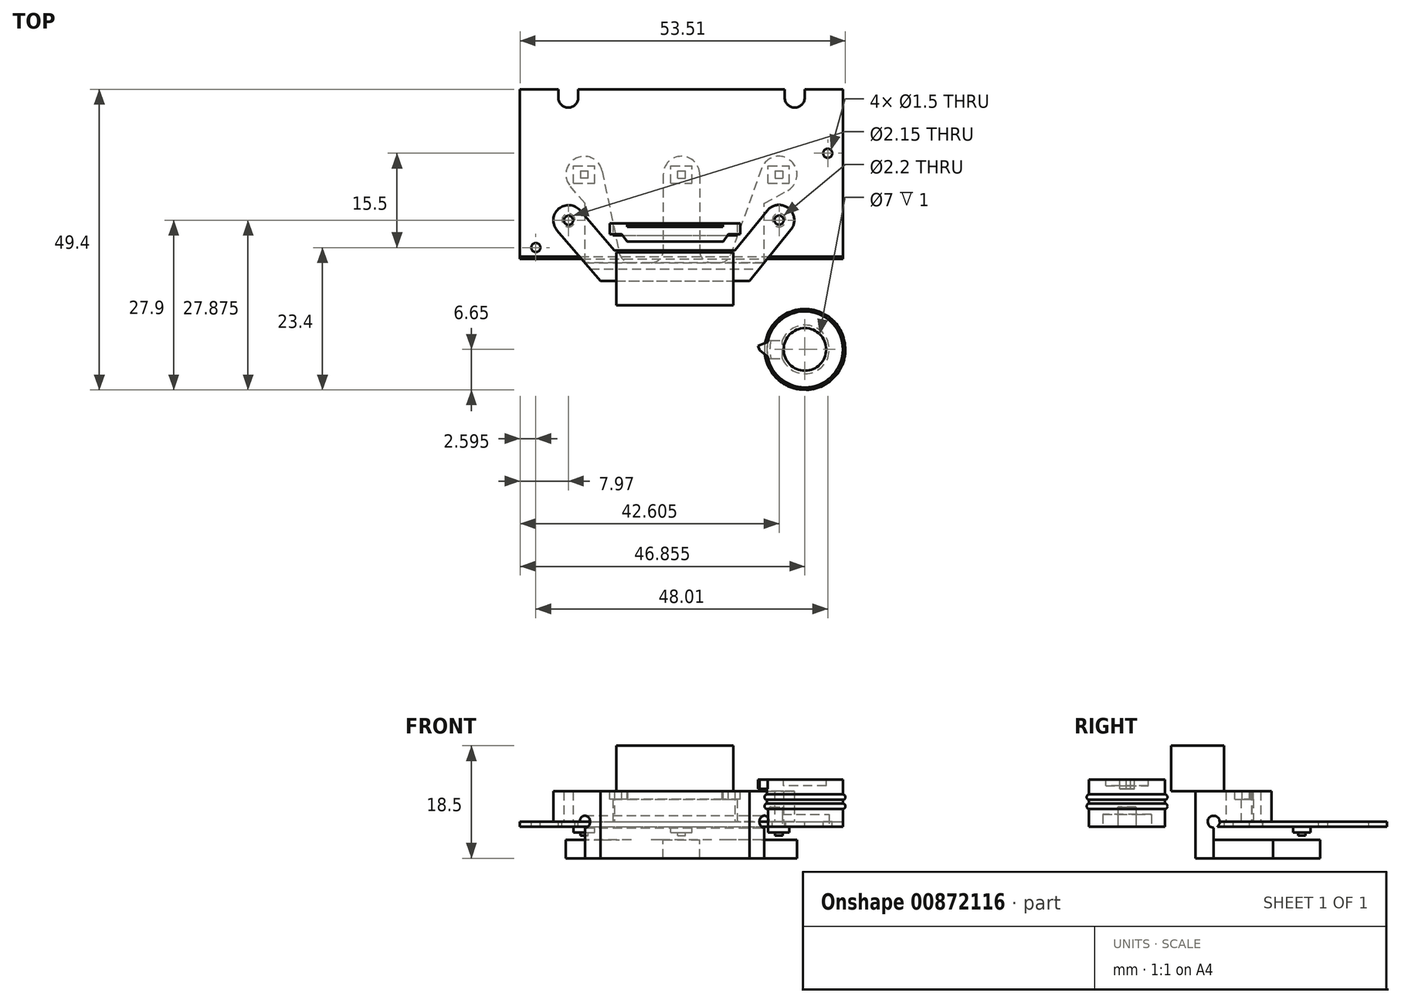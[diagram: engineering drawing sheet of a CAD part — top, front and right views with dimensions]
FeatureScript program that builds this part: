
annotation { "Feature Type Name" : "Feature", "Feature Type Description" : "" }
export const myFeature = defineFeature(function(context is Context, id is Id, definition is map)
    precondition{}
    {
        {
            var Q0;
            Q0=qCreatedBy(makeId("Top.planeOp"),FACE);
            var sketch = newSketch(context, id + "F0", { "sketchPlane" : qUnion([Q0])});
            skLineSegment(sketch, "E0.bottom", {"start": v(-26.56, 14) * mm, "end": v(26.56, 14) * mm});
            skLineSegment(sketch, "E0.top", {"start": v(-26.56, -14) * mm, "end": v(26.55, -14) * mm});
            skLineSegment(sketch, "E0.left", {"start": v(-26.55, 14) * mm, "end": v(-26.56, -14) * mm});
            skLineSegment(sketch, "E0.right", {"start": v(26.56, 14) * mm, "end": v(26.55, -14) * mm});
            skLineSegment(sketch, "E1", {"start": v(-26.56, 14) * mm, "end": v(26.56, -14) * mm, "construction": true});
            skSolve(sketch);
        }
        {
            var Q0;
            Q0 = qSketchRegion(id + "F0", true);
            extrude(context, id + "F1", {"entities" : qUnion([Q0]), "depth" : .8 * mm, "offsetDistance" : 25 * mm});
        }
        {
            var Q0;
            Q0=makeQuery(id+"F1.opExtrude","CAP_FACE",FACE,{"disambiguationData":[OSD([sQuery(id+"F0.wireOp",EDGE,"E0.bottom"),sQuery(id+"F0.wireOp",EDGE,"E0.top"),sQuery(id+"F0.wireOp",EDGE,"E0.left"),sQuery(id+"F0.wireOp",EDGE,"E0.right")])],"isStart":false});
            var sketch = newSketch(context, id + "F2", { "sketchPlane" : qUnion([Q0])});
            skArc(sketch, "E2", {"start": v(16.99, 12.63) * mm, "mid": v(18.62, 11) * mm, "end": v(20.26, 12.63) * mm});
            skArc(sketch, "E3", {"start": v(-20.26, 12.63) * mm, "mid": v(-18.62, 11) * mm, "end": v(-16.98, 12.63) * mm});
            skCircle(sketch, "E4", {"center": v(-18.58, -7.53) * mm, "radius": 1.07 * mm});
            skCircle(sketch, "E5", {"center": v(16.06, -7.5) * mm, "radius": 1.1 * mm});
            skCircle(sketch, "E6", {"center": v(24.05, 3.5) * mm, "radius": 0.75 * mm});
            skCircle(sketch, "E7", {"center": v(-23.96, -12) * mm, "radius": 0.75 * mm});
            skLineSegment(sketch, "E8", {"start": v(16.58, 11) * mm, "end": v(20.98, 11) * mm, "construction": true});
            skLineSegment(sketch, "E9", {"start": v(16.99, 14) * mm, "end": v(20.26, 14) * mm});
            skLineSegment(sketch, "E10.trimOffspring", {"start": v(16.99, 12.63) * mm, "end": v(16.99, 14) * mm});
            skLineSegment(sketch, "E11.trimOffspring", {"start": v(20.26, 12.63) * mm, "end": v(20.26, 14) * mm});
            skLineSegment(sketch, "E12", {"start": v(-16.98, 14) * mm, "end": v(-16.98, 12.63) * mm});
            skLineSegment(sketch, "E13", {"start": v(-20.26, 14) * mm, "end": v(-20.26, 12.63) * mm});
            skLineSegment(sketch, "E14", {"start": v(-20.26, 14) * mm, "end": v(-16.98, 14) * mm});
            skLineSegment(sketch, "E15", {"start": v(24.8, 5.15) * mm, "end": v(24.8, 1.76) * mm, "construction": true});
            skLineSegment(sketch, "E16", {"start": v(22, 2.75) * mm, "end": v(26.48, 2.75) * mm, "construction": true});
            skLineSegment(sketch, "E17", {"start": v(10.95, -8.6) * mm, "end": v(16.92, -8.6) * mm, "construction": true});
            skLineSegment(sketch, "E18", {"start": v(17.16, -5.77) * mm, "end": v(17.16, -10.33) * mm, "construction": true});
            skLineSegment(sketch, "E19", {"start": v(-19.66, -5.92) * mm, "end": v(-19.66, -10.32) * mm, "construction": true});
            skLineSegment(sketch, "E20", {"start": v(-21.28, -8.6) * mm, "end": v(-15.46, -8.6) * mm, "construction": true});
            skLineSegment(sketch, "E21", {"start": v(-24.7, -11.2) * mm, "end": v(-24.7, -13.47) * mm, "construction": true});
            skLineSegment(sketch, "E22", {"start": v(-25.52, -12.75) * mm, "end": v(-23.02, -12.75) * mm, "construction": true});
            skSolve(sketch);
        }
        {
            var Q0;
            Q0 = qSketchRegion(id + "F2", true);
            extrude(context, id + "F3", {"entities" : qUnion([Q0]), "operationType" : NewBodyOperationType.REMOVE, "endBound" : BoundingType.THROUGH_ALL, "oppositeDirection" : true, "depth" : 25 * mm, "offsetDistance" : 25 * mm});
        }
        {
            var Q0;
            Q0=makeQuery(id+"F1.opExtrude","CAP_FACE",FACE,{"disambiguationData":[OSD([sQuery(id+"F0.wireOp",EDGE,"E0.bottom"),sQuery(id+"F0.wireOp",EDGE,"E0.top"),sQuery(id+"F0.wireOp",EDGE,"E0.left"),sQuery(id+"F0.wireOp",EDGE,"E0.right")])],"isStart":false});
            var sketch = newSketch(context, id + "F4", { "sketchPlane" : qUnion([Q0])});
            skLineSegment(sketch, "E23.bottom", {"start": v(-11.26, -8) * mm, "end": v(9.14, -8) * mm});
            skLineSegment(sketch, "E23.top", {"start": v(-11.26, -10) * mm, "end": v(9.14, -10) * mm});
            skLineSegment(sketch, "E23.left", {"start": v(-11.26, -8) * mm, "end": v(-11.26, -10) * mm});
            skLineSegment(sketch, "E23.right", {"start": v(9.14, -8) * mm, "end": v(9.14, -10) * mm});
            skSolve(sketch);
        }
        {
            var Q0;
            Q0 = qSketchRegion(id + "F4", true);
            extrude(context, id + "F5", {"entities" : qUnion([Q0]), "depth" : 5 * mm, "offsetDistance" : 25 * mm});
        }
        {
            var Q0;
            Q0=makeQuery(id+"F5.opExtrude","CAP_FACE",FACE,{"disambiguationData":[OSD([sQuery(id+"F4.wireOp",EDGE,"E23.bottom"),sQuery(id+"F4.wireOp",EDGE,"E23.top"),sQuery(id+"F4.wireOp",EDGE,"E23.left"),sQuery(id+"F4.wireOp",EDGE,"E23.right")])],"isStart":false});
            var sketch = newSketch(context, id + "F6", { "sketchPlane" : qUnion([Q0])});
            skLineSegment(sketch, "E24.bottom", {"start": v(-11.26, -10) * mm, "end": v(9.14, -10) * mm});
            skLineSegment(sketch, "E24.top", {"start": v(-8.8, -8.5) * mm, "end": v(6.7, -8.5) * mm});
            skLineSegment(sketch, "E24.left", {"start": v(-11.26, -10) * mm, "end": v(-11.26, -8.5) * mm});
            skLineSegment(sketch, "E24.right", {"start": v(9.14, -10) * mm, "end": v(9.14, -8.5) * mm});
            skLineSegment(sketch, "E25.top", {"start": v(-8.8, -8) * mm, "end": v(-11.26, -8) * mm});
            skLineSegment(sketch, "E25.left", {"start": v(-8.8, -8.5) * mm, "end": v(-8.8, -8) * mm});
            skLineSegment(sketch, "E25.right", {"start": v(-11.26, -8.5) * mm, "end": v(-11.26, -8) * mm});
            skLineSegment(sketch, "E26.bottom", {"start": v(9.14, -8) * mm, "end": v(6.7, -8) * mm});
            skLineSegment(sketch, "E26.left", {"start": v(9.14, -8) * mm, "end": v(9.14, -8.5) * mm});
            skLineSegment(sketch, "E26.right", {"start": v(6.7, -8) * mm, "end": v(6.7, -8.5) * mm});
            skSolve(sketch);
        }
        {
            var Q0;
            Q0 = qSketchRegion(id + "F6", true);
            extrude(context, id + "F7", {"entities" : qUnion([Q0]), "operationType" : NewBodyOperationType.REMOVE, "oppositeDirection" : true, "depth" : 1.3 * mm, "offsetDistance" : 25 * mm});
        }
        {
            var Q0;
            Q0=makeQuery(id+"F5.opExtrude","CAP_FACE",FACE,{"disambiguationData":[OSD([sQuery(id+"F4.wireOp",EDGE,"E23.bottom"),sQuery(id+"F4.wireOp",EDGE,"E23.top"),sQuery(id+"F4.wireOp",EDGE,"E23.left"),sQuery(id+"F4.wireOp",EDGE,"E23.right")])],"isStart":false});
            var sketch = newSketch(context, id + "F8", { "sketchPlane" : qUnion([Q0])});
            skLineSegment(sketch, "E27.bottom", {"start": v(-11.8, -8) * mm, "end": v(-1.06, -8) * mm});
            skLineSegment(sketch, "E27.top", {"start": v(-8.96, -11) * mm, "end": v(6.84, -11) * mm});
            skLineSegment(sketch, "E27.left", {"start": v(-11.8, -8) * mm, "end": v(-11.8, -9.8) * mm});
            skLineSegment(sketch, "E27.right", {"start": v(9.7, -8) * mm, "end": v(9.7, -9.8) * mm});
            skLineSegment(sketch, "E28", {"start": v(-1.06, -10) * mm, "end": v(-1.06, -6.45) * mm, "construction": true});
            skLineSegment(sketch, "E29.0", {"start": v(-8.9, -8.6) * mm, "end": v(6.8, -8.6) * mm});
            skLineSegment(sketch, "E30.0", {"start": v(-8.9, -8.6) * mm, "end": v(-8.9, -8) * mm});
            skLineSegment(sketch, "E31.0", {"start": v(6.8, -8) * mm, "end": v(6.8, -8.6) * mm});
            skLineSegment(sketch, "E32.trimOffspring", {"start": v(6.8, -8) * mm, "end": v(9.7, -8) * mm});
            skLineSegment(sketch, "E33", {"start": v(9.7, -9.8) * mm, "end": v(7.7, -9.8) * mm});
            skLineSegment(sketch, "E34", {"start": v(7.7, -9.8) * mm, "end": v(6.84, -11) * mm});
            skLineSegment(sketch, "E35.MirrorCS", {"start": v(-11.8, -9.8) * mm, "end": v(-9.8, -9.8) * mm});
            skLineSegment(sketch, "E36.MirrorCS", {"start": v(-9.8, -9.8) * mm, "end": v(-8.96, -11) * mm});
            skSolve(sketch);
        }
        {
            var Q0;
            Q0 = qSketchRegion(id + "F8", true);
            var Q1;
            Q1=makeQuery(id+"F7.boolean.opBoolean","COPY",FACE,{"derivedFrom":makeQuery(id+"F7.opExtrude","CAP_FACE",FACE,{"disambiguationData":[OSD([sQuery(id+"F6.wireOp",EDGE,"E24.bottom"),sQuery(id+"F6.wireOp",EDGE,"E24.top"),sQuery(id+"F6.wireOp",EDGE,"E24.left"),sQuery(id+"F6.wireOp",EDGE,"E24.right"),sQuery(id+"F6.wireOp",EDGE,"E25.top"),sQuery(id+"F6.wireOp",EDGE,"E25.left"),sQuery(id+"F6.wireOp",EDGE,"E25.right"),sQuery(id+"F6.wireOp",EDGE,"E26.bottom"),sQuery(id+"F6.wireOp",EDGE,"E26.left"),sQuery(id+"F6.wireOp",EDGE,"E26.right")])],"isStart":false})});
            extrude(context, id + "F9", {"entities" : qUnion([Q0]), "endBound" : BoundingType.UP_TO_SURFACE, "oppositeDirection" : true, "depth" : 25 * mm, "endBoundEntityFace" : qUnion([Q1]), "offsetDistance" : 25 * mm});
        }
        {
            var Q0;
            Q0=makeQuery(id+"F1.opExtrude","CAP_FACE",FACE,{"disambiguationData":[OSD([sQuery(id+"F0.wireOp",EDGE,"E0.bottom"),sQuery(id+"F0.wireOp",EDGE,"E0.top"),sQuery(id+"F0.wireOp",EDGE,"E0.left"),sQuery(id+"F0.wireOp",EDGE,"E0.right")])],"isStart":true});
            var sketch = newSketch(context, id + "F10", { "sketchPlane" : qUnion([Q0])});
            skLineSegment(sketch, "E37.bottom", {"start": v(-17.75, 1.45) * mm, "end": v(-14.26, 1.45) * mm});
            skLineSegment(sketch, "E37.top", {"start": v(-17.75, -1.45) * mm, "end": v(-14.26, -1.45) * mm});
            skLineSegment(sketch, "E37.left", {"start": v(-17.75, 1.45) * mm, "end": v(-17.75, -1.45) * mm});
            skLineSegment(sketch, "E37.right", {"start": v(-14.26, 1.45) * mm, "end": v(-14.26, -1.45) * mm});
            skLineSegment(sketch, "E38.bottom", {"start": v(-1.75, 1.45) * mm, "end": v(1.75, 1.45) * mm});
            skLineSegment(sketch, "E38.top", {"start": v(-1.75, -1.45) * mm, "end": v(1.75, -1.45) * mm});
            skLineSegment(sketch, "E38.left", {"start": v(-1.75, 1.45) * mm, "end": v(-1.75, -1.45) * mm});
            skLineSegment(sketch, "E38.right", {"start": v(1.75, 1.45) * mm, "end": v(1.75, -1.45) * mm});
            skLineSegment(sketch, "E39.bottom", {"start": v(14.26, 1.45) * mm, "end": v(17.75, 1.45) * mm});
            skLineSegment(sketch, "E39.top", {"start": v(14.26, -1.45) * mm, "end": v(17.75, -1.45) * mm});
            skLineSegment(sketch, "E39.left", {"start": v(14.26, 1.45) * mm, "end": v(14.26, -1.45) * mm});
            skLineSegment(sketch, "E39.right", {"start": v(17.75, 1.45) * mm, "end": v(17.75, -1.45) * mm});
            skLineSegment(sketch, "E40", {"start": v(-1.75, 1.45) * mm, "end": v(1.75, -1.45) * mm, "construction": true});
            skSolve(sketch);
        }
        {
            var Q0;
            Q0 = qSketchRegion(id + "F10", true);
            extrude(context, id + "F11", {"entities" : qUnion([Q0]), "depth" : 1 * mm, "offsetDistance" : 25 * mm});
        }
        {
            var Q0;
            Q0=makeQuery(id+"F11.opExtrude","CAP_FACE",FACE,{"disambiguationData":[OSD([sQuery(id+"F10.wireOp",EDGE,"E37.bottom"),sQuery(id+"F10.wireOp",EDGE,"E37.top"),sQuery(id+"F10.wireOp",EDGE,"E37.left"),sQuery(id+"F10.wireOp",EDGE,"E37.right")])],"isStart":false});
            var sketch = newSketch(context, id + "F12", { "sketchPlane" : qUnion([Q0])});
            skPoint(sketch, "E41.firstSnap0", {"position": v(-14.26, 0) * mm});
            skLineSegment(sketch, "E41.top", {"start": v(-16.63, -0.63) * mm, "end": v(-15.38, -0.63) * mm});
            skLineSegment(sketch, "E41.right", {"start": v(-15.38, 0.62) * mm, "end": v(-15.38, -0.63) * mm});
            skLineSegment(sketch, "E42", {"start": v(-17.75, 1.45) * mm, "end": v(-14.26, -1.45) * mm, "construction": true});
            skLineSegment(sketch, "E43", {"start": v(-15.38, 0.62) * mm, "end": v(-16.63, -0.63) * mm, "construction": true});
            skPoint(sketch, "E44", {"position": v(-16, 0) * mm});
            skLineSegment(sketch, "E45", {"start": v(-15.38, 0.62) * mm, "end": v(-16.63, 0.62) * mm});
            skLineSegment(sketch, "E46", {"start": v(-16.63, -0.63) * mm, "end": v(-16.63, 0.62) * mm});
            skLineSegment(sketch, "E47.bottom", {"start": v(-0.62, 0.62) * mm, "end": v(0.62, 0.62) * mm});
            skLineSegment(sketch, "E47.top", {"start": v(-0.62, -0.62) * mm, "end": v(0.62, -0.62) * mm});
            skLineSegment(sketch, "E47.left", {"start": v(-0.62, 0.62) * mm, "end": v(-0.62, -0.62) * mm});
            skLineSegment(sketch, "E47.right", {"start": v(0.62, 0.62) * mm, "end": v(0.62, -0.62) * mm});
            skLineSegment(sketch, "E48", {"start": v(-0.62, 0.62) * mm, "end": v(0.62, -0.62) * mm, "construction": true});
            skLineSegment(sketch, "E49", {"start": v(14.26, 1.45) * mm, "end": v(17.75, -1.45) * mm, "construction": true});
            skLineSegment(sketch, "E50.bottom", {"start": v(15.38, -0.63) * mm, "end": v(16.63, -0.63) * mm});
            skLineSegment(sketch, "E50.top", {"start": v(15.38, 0.62) * mm, "end": v(16.63, 0.62) * mm});
            skLineSegment(sketch, "E50.left", {"start": v(15.38, -0.63) * mm, "end": v(15.38, 0.62) * mm});
            skLineSegment(sketch, "E50.right", {"start": v(16.63, -0.63) * mm, "end": v(16.63, 0.62) * mm});
            skLineSegment(sketch, "E51", {"start": v(15.38, -0.63) * mm, "end": v(16.63, 0.62) * mm, "construction": true});
            skPoint(sketch, "E52", {"position": v(16, 0) * mm});
            skSolve(sketch);
        }
        {
            var Q0;
            Q0 = qSketchRegion(id + "F12", true);
            extrude(context, id + "F13", {"entities" : qUnion([Q0]), "depth" : .5 * mm, "offsetDistance" : 25 * mm});
        }
        {
            var Q0;
            Q0=makeQuery(id+"F1.opExtrude","CAP_FACE",FACE,{"disambiguationData":[OSD([sQuery(id+"F0.wireOp",EDGE,"E0.bottom"),sQuery(id+"F0.wireOp",EDGE,"E0.top"),sQuery(id+"F0.wireOp",EDGE,"E0.left"),sQuery(id+"F0.wireOp",EDGE,"E0.right")])],"isStart":true});
            var sketch = newSketch(context, id + "F14", { "sketchPlane" : qUnion([Q0])});
            skCircle(sketch, "E53", {"center": v(20.3, 28.75) * mm, "radius": 6.25 * mm});
            skLineSegment(sketch, "E54", {"start": v(14.4, 22.5) * mm, "end": v(31.08, 22.5) * mm, "construction": true});
            skLineSegment(sketch, "E55", {"start": v(26.55, 37.01) * mm, "end": v(26.55, 25.34) * mm, "construction": true});
            skSolve(sketch);
        }
        {
            var Q0;
            Q0 = qSketchRegion(id + "F14", true);
            extrude(context, id + "F15", {"entities" : qUnion([Q0]), "oppositeDirection" : true, "depth" : 7.7 * mm, "offsetDistance" : 25 * mm});
        }
        {
            var Q0;
            Q0=makeQuery(id+"F15.opExtrude","CAP_FACE",FACE,{"disambiguationData":[OSD([sQuery(id+"F14.wireOp",EDGE,"E53")])],"isStart":false});
            var sketch = newSketch(context, id + "F16", { "sketchPlane" : qUnion([Q0])});
            skCircle(sketch, "E56", {"center": v(20.3, -28.75) * mm, "radius": 3.5 * mm});
            skSolve(sketch);
        }
        {
            var Q0;
            Q0 = qSketchRegion(id + "F16", true);
            extrude(context, id + "F17", {"entities" : qUnion([Q0]), "operationType" : NewBodyOperationType.REMOVE, "oppositeDirection" : true, "depth" : 1 * mm, "offsetDistance" : 25 * mm});
        }
        {
            var Q0;
            Q0=makeQuery(id+"F15.opExtrude","CAP_FACE",FACE,{"disambiguationData":[OSD([sQuery(id+"F14.wireOp",EDGE,"E53")])],"isStart":true});
            var sketch = newSketch(context, id + "F18", { "sketchPlane" : qUnion([Q0])});
            skCircle(sketch, "E57", {"center": v(20.3, 28.75) * mm, "radius": 4 * mm});
            skSolve(sketch);
        }
        {
            var Q0;
            Q0 = qSketchRegion(id + "F18", true);
            extrude(context, id + "F19", {"entities" : qUnion([Q0]), "operationType" : NewBodyOperationType.REMOVE, "oppositeDirection" : true, "depth" : 2 * mm, "offsetDistance" : 25 * mm});
        }
        {
            var Q0;
            Q0=makeQuery(id+"F15.opExtrude","CAP_FACE",FACE,{"disambiguationData":[OSD([sQuery(id+"F14.wireOp",EDGE,"E53")])],"isStart":true});
            var sketch = newSketch(context, id + "F20", { "sketchPlane" : qUnion([Q0])});
            skLineSegment(sketch, "E58.bottom", {"start": v(14.05, 30.25) * mm, "end": v(16.6, 30.25) * mm});
            skLineSegment(sketch, "E58.top", {"start": v(14.05, 27.25) * mm, "end": v(16.6, 27.25) * mm});
            skLineSegment(sketch, "E58.left", {"start": v(14.05, 30.25) * mm, "end": v(14.05, 27.25) * mm});
            skLineSegment(sketch, "E58.right", {"start": v(16.6, 30.25) * mm, "end": v(16.6, 27.25) * mm});
            skPoint(sketch, "E59", {"position": v(20.3, 28.75) * mm});
            skLineSegment(sketch, "E60", {"start": v(16.6, 28.75) * mm, "end": v(20.3, 28.75) * mm});
            skSolve(sketch);
        }
        {
            var Q0;
            Q0 = qSketchRegion(id + "F20", true);
            extrude(context, id + "F21", {"entities" : qUnion([Q0]), "operationType" : NewBodyOperationType.REMOVE, "oppositeDirection" : true, "depth" : 3.2 * mm, "offsetDistance" : 25 * mm});
        }
        {
            var Q0;
            Q0=makeQuery(id+"F15.opExtrude","CAP_FACE",FACE,{"disambiguationData":[OSD([sQuery(id+"F14.wireOp",EDGE,"E53")])],"isStart":false});
            var sketch = newSketch(context, id + "F22", { "sketchPlane" : qUnion([Q0])});
            skArc(sketch, "E61.0", {"start": v(14.17, -27.55) * mm, "mid": v(14.05, -28.75) * mm, "end": v(14.17, -29.95) * mm});
            skLineSegment(sketch, "E62", {"start": v(14.17, -27.55) * mm, "end": v(12.58, -28.16) * mm});
            skLineSegment(sketch, "E63", {"start": v(12.58, -28.16) * mm, "end": v(12.85, -28.87) * mm});
            skLineSegment(sketch, "E64", {"start": v(12.85, -28.87) * mm, "end": v(14.17, -29.95) * mm});
            skSolve(sketch);
        }
        {
            var Q0;
            Q0 = qSketchRegion(id + "F22", true);
            extrude(context, id + "F23", {"entities" : qUnion([Q0]), "operationType" : NewBodyOperationType.ADD, "oppositeDirection" : true, "depth" : 1.5 * mm, "offsetDistance" : 25 * mm});
        }
        {
            var Q0;
            Q0=makeQuery(id+"F23.boolean.opBoolean","MERGE",FACE,{"derivedFrom":[makeQuery(id+"F15.opExtrude","CAP_FACE",FACE,{"disambiguationData":[OSD([sQuery(id+"F14.wireOp",EDGE,"E53")])],"isStart":false}),makeQuery(id+"F23.opExtrude","CAP_FACE",FACE,{"disambiguationData":[OSD([sQuery(id+"F22.wireOp",EDGE,"E61.0"),sQuery(id+"F22.wireOp",EDGE,"E62"),sQuery(id+"F22.wireOp",EDGE,"E63"),sQuery(id+"F22.wireOp",EDGE,"E64")])],"isStart":true})]});
            var sketch = newSketch(context, id + "F24", { "sketchPlane" : qUnion([Q0])});
            skLineSegment(sketch, "E65", {"start": v(20.3, -19.73) * mm, "end": v(20.3, -37.77) * mm});
            skPoint(sketch, "E66", {"position": v(20.3, -28.75) * mm});
            skSolve(sketch);
        }
        {
            var Q0;
            Q0=sQuery(id+"F24.wireOp",EDGE,"E65");
            cPlane(context, id + "F25", {"entities" : qUnion([Q0]), "cplaneType" : CPlaneType.MID_PLANE, "offset" : 25 * mm, "width" : 150 * mm, "height" : 150 * mm});
        }
        {
            var Q0;
            Q0=qCreatedBy(id+"F25.planeOp",FACE);
            var sketch = newSketch(context, id + "F26", { "sketchPlane" : qUnion([Q0])});
            skCircle(sketch, "E67", {"center": v(26.5, 4.85) * mm, "radius": 0.45 * mm});
            skCircle(sketch, "E68", {"center": v(26.5, 3.35) * mm, "radius": 0.45 * mm});
            skLineSegment(sketch, "E69", {"start": v(20.3, 8.47) * mm, "end": v(20.3, -0.14) * mm, "construction": true});
            skLineSegment(sketch, "E70", {"start": v(25.58, 4.4) * mm, "end": v(27.51, 4.4) * mm, "construction": true});
            skSolve(sketch);
        }
        {
            var Q0;
            Q0 = qSketchRegion(id + "F26", true);
            var Q1;
            Q1=sQuery(id+"F26.wireOp",EDGE,"E69");
            revolve(context, id + "F27", {"operationType" : NewBodyOperationType.ADD, "surfaceOperationType" : NewSurfaceOperationType.NEW, "entities" : qUnion([Q0]), "axis" : qUnion([Q1]), "revolveType" : RevolveType.FULL});
        }
        {
            var Q0;
            Q0=makeQuery(id+"F1.opExtrude","CAP_FACE",FACE,{"disambiguationData":[OSD([sQuery(id+"F0.wireOp",EDGE,"E0.bottom"),sQuery(id+"F0.wireOp",EDGE,"E0.top"),sQuery(id+"F0.wireOp",EDGE,"E0.left"),sQuery(id+"F0.wireOp",EDGE,"E0.right")])],"isStart":false});
            var sketch = newSketch(context, id + "F28", { "sketchPlane" : qUnion([Q0])});
            skArc(sketch, "E71", {"start": v(18, -9.07) * mm, "mid": v(17.63, -5.55) * mm, "end": v(14.1, -5.93) * mm});
            skArc(sketch, "E72", {"start": v(-16.68, -5.9) * mm, "mid": v(-20.2, -5.63) * mm, "end": v(-20.48, -9.15) * mm});
            skLineSegment(sketch, "E73.bottom", {"start": v(-11, -12.5) * mm, "end": v(8.8, -12.5) * mm});
            skLineSegment(sketch, "E73.top", {"start": v(-13.3, -17.5) * mm, "end": v(11.2, -17.5) * mm});
            skLineSegment(sketch, "E73.left", {"start": v(-13.3, -12.5) * mm, "end": v(-13.3, -17.5) * mm, "construction": true});
            skLineSegment(sketch, "E73.right", {"start": v(11.2, -12.5) * mm, "end": v(11.2, -17.5) * mm, "construction": true});
            skLineSegment(sketch, "E74", {"start": v(-20.48, -9.15) * mm, "end": v(-13.3, -17.5) * mm});
            skLineSegment(sketch, "E75", {"start": v(-16.68, -5.9) * mm, "end": v(-11, -12.5) * mm});
            skLineSegment(sketch, "E76", {"start": v(-1.06, -17.5) * mm, "end": v(-1.06, -14.15) * mm, "construction": true});
            skLineSegment(sketch, "E77", {"start": v(11.2, -17.5) * mm, "end": v(18, -9.07) * mm});
            skLineSegment(sketch, "E78", {"start": v(14.1, -5.93) * mm, "end": v(8.8, -12.5) * mm});
            skSolve(sketch);
        }
        {
            var Q0;
            Q0 = qSketchRegion(id + "F28", true);
            extrude(context, id + "F29", {"entities" : qUnion([Q0]), "depth" : 5 * mm, "offsetDistance" : 25 * mm});
        }
        {
            var Q0;
            Q0=makeQuery(id+"F29.opExtrude","CAP_FACE",FACE,{"disambiguationData":[OSD([sQuery(id+"F28.wireOp",EDGE,"E71"),sQuery(id+"F28.wireOp",EDGE,"E72"),sQuery(id+"F28.wireOp",EDGE,"E73.bottom"),sQuery(id+"F28.wireOp",EDGE,"E73.top"),sQuery(id+"F28.wireOp",EDGE,"E74"),sQuery(id+"F28.wireOp",EDGE,"E75"),sQuery(id+"F28.wireOp",EDGE,"E77"),sQuery(id+"F28.wireOp",EDGE,"E78")])],"isStart":true});
            var sketch = newSketch(context, id + "F30", { "sketchPlane" : qUnion([Q0])});
            skCircle(sketch, "E79", {"center": v(-18.58, 7.53) * mm, "radius": 0.75 * mm});
            skCircle(sketch, "E80", {"center": v(16.06, 7.5) * mm, "radius": 0.75 * mm});
            skSolve(sketch);
        }
        {
            var Q0;
            Q0 = qSketchRegion(id + "F30", true);
            extrude(context, id + "F31", {"entities" : qUnion([Q0]), "operationType" : NewBodyOperationType.REMOVE, "endBound" : BoundingType.THROUGH_ALL, "oppositeDirection" : true, "depth" : 25 * mm, "offsetDistance" : 25 * mm});
        }
        {
            var Q0;
            Q0=makeQuery(id+"F29.opExtrude","CAP_FACE",FACE,{"disambiguationData":[OSD([sQuery(id+"F28.wireOp",EDGE,"E71"),sQuery(id+"F28.wireOp",EDGE,"E72"),sQuery(id+"F28.wireOp",EDGE,"E73.bottom"),sQuery(id+"F28.wireOp",EDGE,"E73.top"),sQuery(id+"F28.wireOp",EDGE,"E74"),sQuery(id+"F28.wireOp",EDGE,"E75"),sQuery(id+"F28.wireOp",EDGE,"E77"),sQuery(id+"F28.wireOp",EDGE,"E78")])],"isStart":true});
            var sketch = newSketch(context, id + "F32", { "sketchPlane" : qUnion([Q0])});
            skLineSegment(sketch, "E81.bottom", {"start": v(11.2, 17.5) * mm, "end": v(-13.3, 17.5) * mm});
            skLineSegment(sketch, "E81.top", {"start": v(11.2, 14.5) * mm, "end": v(-13.3, 14.5) * mm});
            skLineSegment(sketch, "E81.left", {"start": v(11.2, 17.5) * mm, "end": v(11.2, 14.5) * mm, "construction": true});
            skLineSegment(sketch, "E81.right", {"start": v(-13.3, 17.5) * mm, "end": v(-13.3, 14.5) * mm, "construction": true});
            skLineSegment(sketch, "E82", {"start": v(11.2, 14.5) * mm, "end": v(13.62, 14.5) * mm});
            skLineSegment(sketch, "E83", {"start": v(13.62, 14.5) * mm, "end": v(11.2, 17.5) * mm});
            skLineSegment(sketch, "E84", {"start": v(-13.3, 14.5) * mm, "end": v(-15.88, 14.5) * mm});
            skLineSegment(sketch, "E85", {"start": v(-15.88, 14.5) * mm, "end": v(-13.3, 17.5) * mm});
            skSolve(sketch);
        }
        {
            var Q0;
            Q0=makeQuery(id+"F32.imprint","IMPRINT",FACE,{"disambiguationData":[TD([[makeQuery(id+"F32.imprint","IMPRINT",EDGE,{"derivedFrom":sQuery(id+"F32.wireOp",EDGE,"E81.bottom")}),-1.0]])]});
            var Q1;
            Q1=sQuery(id+"F32.wireOp",EDGE,"E81.left");
            var Q2;
            Q2=sQuery(id+"F32.wireOp",EDGE,"E81.right");
            extrude(context, id + "F33", {"entities" : qUnion([Q0]), "operationType" : NewBodyOperationType.ADD, "surfaceOperationType" : NewSurfaceOperationType.ADD, "surfaceEntities" : qUnion([Q1, Q2]), "depth" : 3 * mm, "offsetDistance" : 25 * mm});
        }
        {
            var Q0;
            Q0=makeQuery(id+"F33.opExtrude","CAP_FACE",FACE,{"disambiguationData":[OSD([sQuery(id+"F32.wireOp",EDGE,"E81.bottom"),sQuery(id+"F32.wireOp",EDGE,"E81.top"),sQuery(id+"F32.wireOp",EDGE,"E82"),sQuery(id+"F32.wireOp",EDGE,"E83"),sQuery(id+"F32.wireOp",EDGE,"E84"),sQuery(id+"F32.wireOp",EDGE,"E85")])],"isStart":false});
            var sketch = newSketch(context, id + "F34", { "sketchPlane" : qUnion([Q0])});
            skArc(sketch, "E86", {"start": v(-3, 0) * mm, "mid": v(0, -3) * mm, "end": v(3, 0) * mm});
            skArc(sketch, "E87", {"start": v(-18.28, 1.96) * mm, "mid": v(-17.33, -2.69) * mm, "end": v(-13.07, -0.62) * mm});
            skArc(sketch, "E88", {"start": v(13.18, -1.01) * mm, "mid": v(17.95, -2.28) * mm, "end": v(17.46, 2.63) * mm});
            skLineSegment(sketch, "E89", {"start": v(17.75, 1.45) * mm, "end": v(14.25, -1.45) * mm, "construction": true});
            skLineSegment(sketch, "E90", {"start": v(-17.75, 1.45) * mm, "end": v(-14.26, -1.45) * mm, "construction": true});
            skLineSegment(sketch, "E91.0", {"start": v(7.62, 14.5) * mm, "end": v(3, 14.5) * mm});
            skLineSegment(sketch, "E91.1", {"start": v(-15.88, 14.5) * mm, "end": v(-13.3, 17.5) * mm});
            skLineSegment(sketch, "E91.2", {"start": v(-13.3, 17.5) * mm, "end": v(11.2, 17.5) * mm});
            skLineSegment(sketch, "E91.3", {"start": v(11.2, 17.5) * mm, "end": v(13.62, 14.5) * mm});
            skLineSegment(sketch, "E92", {"start": v(-13.07, -0.62) * mm, "end": v(-9.88, 14.5) * mm});
            skLineSegment(sketch, "E93", {"start": v(-3, 0) * mm, "end": v(-3, 14.5) * mm});
            skLineSegment(sketch, "E94", {"start": v(3, 0) * mm, "end": v(3, 14.5) * mm});
            skLineSegment(sketch, "E95", {"start": v(-15.88, 14.5) * mm, "end": v(-15.88, 4.75) * mm});
            skLineSegment(sketch, "E96", {"start": v(-15.88, 4.75) * mm, "end": v(-18.28, 1.96) * mm});
            skLineSegment(sketch, "E97", {"start": v(13.18, -1.01) * mm, "end": v(7.62, 14.5) * mm});
            skLineSegment(sketch, "E98", {"start": v(13.62, 14.5) * mm, "end": v(13.62, 4.75) * mm});
            skLineSegment(sketch, "E99", {"start": v(13.62, 4.75) * mm, "end": v(17.46, 2.63) * mm});
            skPoint(sketch, "E100.orphan", {"position": v(22.21, 0) * mm});
            skLineSegment(sketch, "E101.trimOffspring", {"start": v(-3, 14.5) * mm, "end": v(-9.88, 14.5) * mm});
            skSolve(sketch);
        }
        {
            var Q0;
            Q0 = qSketchRegion(id + "F34", true);
            extrude(context, id + "F35", {"entities" : qUnion([Q0]), "operationType" : NewBodyOperationType.ADD, "depth" : 3 * mm, "offsetDistance" : 25 * mm});
        }
        {
            var Q0;
            Q0=qCreatedBy(makeId("Right.planeOp"),FACE);
            var sketch = newSketch(context, id + "F36", { "sketchPlane" : qUnion([Q0])});
            skCircle(sketch, "E102", {"center": v(-14.5, 0.8) * mm, "radius": 1 * mm});
            skSolve(sketch);
        }
        {
            var Q0;
            Q0 = qSketchRegion(id + "F36", true);
            extrude(context, id + "F37", {"entities" : qUnion([Q0]), "operationType" : NewBodyOperationType.REMOVE, "endBound" : BoundingType.THROUGH_ALL, "oppositeDirection" : true, "depth" : 25 * mm, "offsetDistance" : 25 * mm, "hasSecondDirection" : true, "secondDirectionBound" : BoundingType.THROUGH_ALL, "secondDirectionOppositeDirection" : false, "secondDirectionDepth" : 25 * mm});
        }
        {
            var Q0;
            Q0=makeQuery(id+"F35.opExtrude","SWEPT_EDGE",EDGE,{"disambiguationData":[OSD([sQuery(id+"F32.wireOp",EDGE,"E81.top"),sQuery(id+"F32.wireOp",EDGE,"E82"),sQuery(id+"F32.wireOp",EDGE,"E84"),sQuery(id+"F34.wireOp",EDGE,"E92"),sQuery(id+"F34.wireOp",EDGE,"E101.trimOffspring")])]});
            var Q1;
            Q1=makeQuery(id+"F35.opExtrude","SWEPT_EDGE",EDGE,{"disambiguationData":[OSD([sQuery(id+"F32.wireOp",EDGE,"E81.top"),sQuery(id+"F32.wireOp",EDGE,"E82"),sQuery(id+"F32.wireOp",EDGE,"E84"),sQuery(id+"F34.wireOp",EDGE,"E93"),sQuery(id+"F34.wireOp",EDGE,"E101.trimOffspring")])]});
            var Q2;
            Q2=makeQuery(id+"F35.opExtrude","SWEPT_EDGE",EDGE,{"disambiguationData":[OSD([sQuery(id+"F32.wireOp",EDGE,"E81.top"),sQuery(id+"F32.wireOp",EDGE,"E82"),sQuery(id+"F32.wireOp",EDGE,"E84"),sQuery(id+"F34.wireOp",EDGE,"E91.0"),sQuery(id+"F34.wireOp",EDGE,"E94")])]});
            var Q3;
            Q3=makeQuery(id+"F35.opExtrude","SWEPT_EDGE",EDGE,{"disambiguationData":[OSD([sQuery(id+"F32.wireOp",EDGE,"E81.top"),sQuery(id+"F32.wireOp",EDGE,"E82"),sQuery(id+"F32.wireOp",EDGE,"E84"),sQuery(id+"F34.wireOp",EDGE,"E91.0"),sQuery(id+"F34.wireOp",EDGE,"E97")])]});
            fillet(context, id + "F38", {"entities" : qUnion([Q0, Q1, Q2, Q3]), "radius" : 2 * mm, "tangentPropagation" : true, "allowEdgeOverflow" : false});
        }
        {
            var Q0;
            Q0=makeQuery(id+"F29.opExtrude","CAP_FACE",FACE,{"disambiguationData":[OSD([sQuery(id+"F28.wireOp",EDGE,"E71"),sQuery(id+"F28.wireOp",EDGE,"E72"),sQuery(id+"F28.wireOp",EDGE,"E73.bottom"),sQuery(id+"F28.wireOp",EDGE,"E73.top"),sQuery(id+"F28.wireOp",EDGE,"E74"),sQuery(id+"F28.wireOp",EDGE,"E75"),sQuery(id+"F28.wireOp",EDGE,"E77"),sQuery(id+"F28.wireOp",EDGE,"E78")])],"isStart":false});
            var sketch = newSketch(context, id + "F39", { "sketchPlane" : qUnion([Q0])});
            skLineSegment(sketch, "E103.bottom", {"start": v(8.8, -12.5) * mm, "end": v(-11, -12.5) * mm});
            skLineSegment(sketch, "E103.top", {"start": v(8.8, -22.5) * mm, "end": v(-11, -22.5) * mm});
            skLineSegment(sketch, "E103.left", {"start": v(8.8, -12.5) * mm, "end": v(8.8, -22.5) * mm});
            skLineSegment(sketch, "E103.right", {"start": v(-11, -12.5) * mm, "end": v(-11, -22.5) * mm});
            skSolve(sketch);
        }
        {
            var Q0;
            Q0 = qSketchRegion(id + "F39", true);
            extrude(context, id + "F40", {"entities" : qUnion([Q0]), "operationType" : NewBodyOperationType.ADD, "depth" : 7 * mm, "offsetDistance" : 25 * mm});
        }
        {
            var Q0;
            Q0=makeQuery(id+"F40.opExtrude","CAP_FACE",FACE,{"disambiguationData":[OSD([sQuery(id+"F39.wireOp",EDGE,"E103.bottom"),sQuery(id+"F39.wireOp",EDGE,"E103.top"),sQuery(id+"F39.wireOp",EDGE,"E103.left"),sQuery(id+"F39.wireOp",EDGE,"E103.right")])],"isStart":false});
            var sketch = newSketch(context, id + "F41", { "sketchPlane" : qUnion([Q0])});
            skLineSegment(sketch, "E104.bottom", {"start": v(-11, -12.5) * mm, "end": v(8.8, -12.5) * mm});
            skLineSegment(sketch, "E104.top", {"start": v(-11, -22.5) * mm, "end": v(8.8, -22.5) * mm});
            skLineSegment(sketch, "E104.left", {"start": v(-11, -12.5) * mm, "end": v(-11, -22.5) * mm});
            skLineSegment(sketch, "E104.right", {"start": v(8.8, -12.5) * mm, "end": v(8.8, -22.5) * mm});
            skSolve(sketch);
        }
        {
            var Q0;
            Q0 = qSketchRegion(id + "F41", true);
            extrude(context, id + "F42", {"entities" : qUnion([Q0]), "operationType" : NewBodyOperationType.ADD, "depth" : .5 * mm, "offsetDistance" : 25 * mm});
        }
        {
            var Q0;
            Q0=makeQuery(id+"F42.opExtrude","CAP_FACE",FACE,{"disambiguationData":[OSD([sQuery(id+"F41.wireOp",EDGE,"E104.bottom"),sQuery(id+"F41.wireOp",EDGE,"E104.top"),sQuery(id+"F41.wireOp",EDGE,"E104.left"),sQuery(id+"F41.wireOp",EDGE,"E104.right")])],"isStart":false});
            var sketch = newSketch(context, id + "F43", { "sketchPlane" : qUnion([Q0])});
            skLineSegment(sketch, "E105.0", {"start": v(-10.7, -12.8) * mm, "end": v(-10.7, -21.5) * mm});
            skLineSegment(sketch, "E106.0", {"start": v(-10.7, -12.8) * mm, "end": v(8.5, -12.8) * mm});
            skLineSegment(sketch, "E107.0", {"start": v(8.5, -21.5) * mm, "end": v(-10.7, -21.5) * mm});
            skLineSegment(sketch, "E108.0", {"start": v(8.5, -12.8) * mm, "end": v(8.5, -21.5) * mm});
            skSolve(sketch);
        }
        {
            var Q0;
            Q0=makeQuery(id+"F43.imprint","IMPRINT",FACE,{"disambiguationData":[TD([[makeQuery(id+"F43.imprint","IMPRINT",EDGE,{"derivedFrom":sQuery(id+"F43.wireOp",EDGE,"E105.0")}),-1.0]])]});
            var Q1;
            {var subQ0=sQuery(id+"F28.wireOp",EDGE,"E78");var subQ1=sQuery(id+"F28.wireOp",EDGE,"E71");var subQ3=sQuery(id+"F28.wireOp",EDGE,"E73.top");var subQ4=sQuery(id+"F28.wireOp",EDGE,"E73.bottom");var subQ5=sQuery(id+"F28.wireOp",EDGE,"E77");Q1=makeQuery(id+"F40.boolean.opBoolean","SPLIT",FACE,{"disambiguationData":[TD([makeQuery(id+"F29.opExtrude","SWEPT_FACE",FACE,{"disambiguationData":[OSD([subQ1])]})])],"derivedFrom":makeQuery(id+"F29.opExtrude","CAP_FACE",FACE,{"disambiguationData":[OSD([subQ1,sQuery(id+"F28.wireOp",EDGE,"E72"),subQ4,subQ3,sQuery(id+"F28.wireOp",EDGE,"E74"),sQuery(id+"F28.wireOp",EDGE,"E75"),subQ5,subQ0])],"isStart":false})});}
            extrude(context, id + "F44", {"entities" : qUnion([Q0]), "operationType" : NewBodyOperationType.REMOVE, "endBound" : BoundingType.UP_TO_SURFACE, "oppositeDirection" : true, "depth" : 25 * mm, "endBoundEntityFace" : qUnion([Q1]), "offsetDistance" : 25 * mm});
        }
    });
